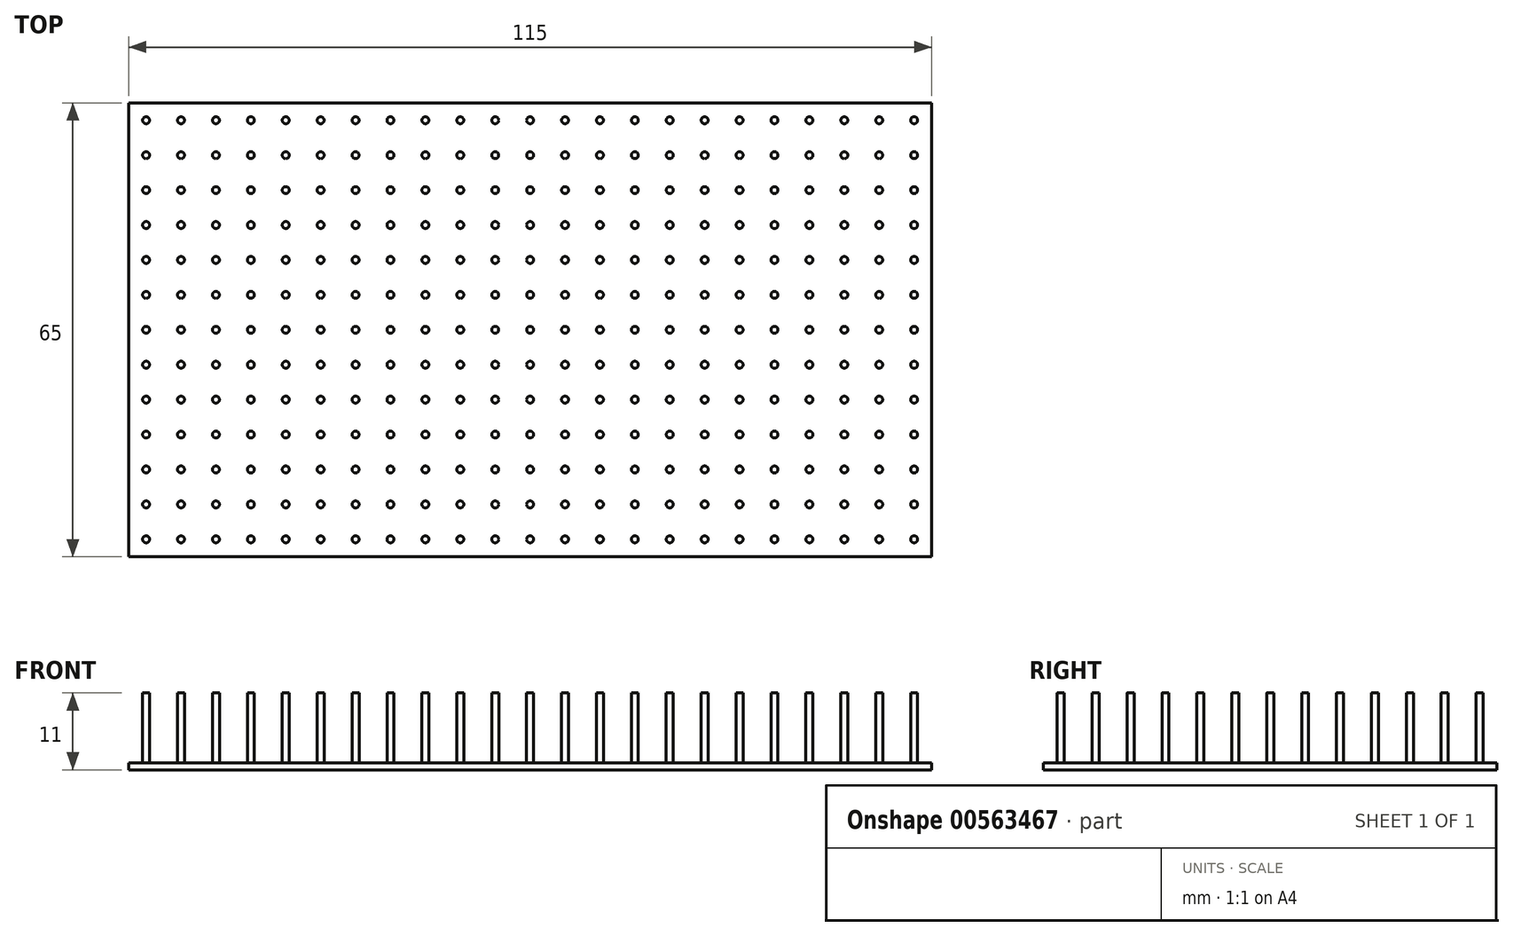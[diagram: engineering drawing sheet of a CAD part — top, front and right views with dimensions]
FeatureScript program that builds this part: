
annotation { "Feature Type Name" : "Feature", "Feature Type Description" : "" }
export const myFeature = defineFeature(function(context is Context, id is Id, definition is map)
    precondition{}
    {
        {
            var Q0;
            Q0=qCreatedBy(makeId("Top.planeOp"),FACE);
            var sketch = newSketch(context, id + "F0", { "sketchPlane" : qUnion([Q0])});
            skLineSegment(sketch, "E0.bottom", {"start": v(0, 0) * mm, "end": v(115, 0) * mm});
            skLineSegment(sketch, "E0.top", {"start": v(0, 65) * mm, "end": v(115, 65) * mm});
            skLineSegment(sketch, "E0.left", {"start": v(0, 0) * mm, "end": v(0, 65) * mm});
            skLineSegment(sketch, "E0.right", {"start": v(115, 0) * mm, "end": v(115, 65) * mm});
            skSolve(sketch);
        }
        {
            var Q0;
            Q0 = qSketchRegion(id + "F0", true);
            extrude(context, id + "F1", {"entities" : qUnion([Q0]), "depth" : 1 * mm, "offsetDistance" : 25 * mm});
        }
        {
            var Q0;
            Q0=makeQuery(id+"F1.opExtrude","CAP_FACE",FACE,{"disambiguationData":[OSD([sQuery(id+"F0.wireOp",EDGE,"E0.bottom"),sQuery(id+"F0.wireOp",EDGE,"E0.top"),sQuery(id+"F0.wireOp",EDGE,"E0.left"),sQuery(id+"F0.wireOp",EDGE,"E0.right")])],"isStart":false});
            var sketch = newSketch(context, id + "F2", { "sketchPlane" : qUnion([Q0])});
            skCircle(sketch, "E1", {"center": v(2.5, 2.5) * mm, "radius": 0.5 * mm});
            skCircle(sketch, "E2.0.1.0", {"center": v(2.5, 7.5) * mm, "radius": 0.5 * mm});
            skCircle(sketch, "E2.0.2.0", {"center": v(2.5, 12.5) * mm, "radius": 0.5 * mm});
            skCircle(sketch, "E2.0.3.0", {"center": v(2.5, 17.5) * mm, "radius": 0.5 * mm});
            skCircle(sketch, "E2.0.4.0", {"center": v(2.5, 22.5) * mm, "radius": 0.5 * mm});
            skCircle(sketch, "E2.0.5.0", {"center": v(2.5, 27.5) * mm, "radius": 0.5 * mm});
            skCircle(sketch, "E2.0.6.0", {"center": v(2.5, 32.5) * mm, "radius": 0.5 * mm});
            skCircle(sketch, "E2.0.7.0", {"center": v(2.5, 37.5) * mm, "radius": 0.5 * mm});
            skCircle(sketch, "E2.0.8.0", {"center": v(2.5, 42.5) * mm, "radius": 0.5 * mm});
            skCircle(sketch, "E2.0.9.0", {"center": v(2.5, 47.5) * mm, "radius": 0.5 * mm});
            skCircle(sketch, "E2.0.10.0", {"center": v(2.5, 52.5) * mm, "radius": 0.5 * mm});
            skCircle(sketch, "E2.0.11.0", {"center": v(2.5, 57.5) * mm, "radius": 0.5 * mm});
            skCircle(sketch, "E2.0.12.0", {"center": v(2.5, 62.5) * mm, "radius": 0.5 * mm});
            skCircle(sketch, "E2.1.0.0", {"center": v(7.5, 2.5) * mm, "radius": 0.5 * mm});
            skCircle(sketch, "E2.1.1.0", {"center": v(7.5, 7.5) * mm, "radius": 0.5 * mm});
            skCircle(sketch, "E2.1.2.0", {"center": v(7.5, 12.5) * mm, "radius": 0.5 * mm});
            skCircle(sketch, "E2.1.3.0", {"center": v(7.5, 17.5) * mm, "radius": 0.5 * mm});
            skCircle(sketch, "E2.1.4.0", {"center": v(7.5, 22.5) * mm, "radius": 0.5 * mm});
            skCircle(sketch, "E2.1.5.0", {"center": v(7.5, 27.5) * mm, "radius": 0.5 * mm});
            skCircle(sketch, "E2.1.6.0", {"center": v(7.5, 32.5) * mm, "radius": 0.5 * mm});
            skCircle(sketch, "E2.1.7.0", {"center": v(7.5, 37.5) * mm, "radius": 0.5 * mm});
            skCircle(sketch, "E2.1.8.0", {"center": v(7.5, 42.5) * mm, "radius": 0.5 * mm});
            skCircle(sketch, "E2.1.9.0", {"center": v(7.5, 47.5) * mm, "radius": 0.5 * mm});
            skCircle(sketch, "E2.1.10.0", {"center": v(7.5, 52.5) * mm, "radius": 0.5 * mm});
            skCircle(sketch, "E2.1.11.0", {"center": v(7.5, 57.5) * mm, "radius": 0.5 * mm});
            skCircle(sketch, "E2.1.12.0", {"center": v(7.5, 62.5) * mm, "radius": 0.5 * mm});
            skCircle(sketch, "E2.2.0.0", {"center": v(12.5, 2.5) * mm, "radius": 0.5 * mm});
            skCircle(sketch, "E2.2.1.0", {"center": v(12.5, 7.5) * mm, "radius": 0.5 * mm});
            skCircle(sketch, "E2.2.2.0", {"center": v(12.5, 12.5) * mm, "radius": 0.5 * mm});
            skCircle(sketch, "E2.2.3.0", {"center": v(12.5, 17.5) * mm, "radius": 0.5 * mm});
            skCircle(sketch, "E2.2.4.0", {"center": v(12.5, 22.5) * mm, "radius": 0.5 * mm});
            skCircle(sketch, "E2.2.5.0", {"center": v(12.5, 27.5) * mm, "radius": 0.5 * mm});
            skCircle(sketch, "E2.2.6.0", {"center": v(12.5, 32.5) * mm, "radius": 0.5 * mm});
            skCircle(sketch, "E2.2.7.0", {"center": v(12.5, 37.5) * mm, "radius": 0.5 * mm});
            skCircle(sketch, "E2.2.8.0", {"center": v(12.5, 42.5) * mm, "radius": 0.5 * mm});
            skCircle(sketch, "E2.2.9.0", {"center": v(12.5, 47.5) * mm, "radius": 0.5 * mm});
            skCircle(sketch, "E2.2.10.0", {"center": v(12.5, 52.5) * mm, "radius": 0.5 * mm});
            skCircle(sketch, "E2.2.11.0", {"center": v(12.5, 57.5) * mm, "radius": 0.5 * mm});
            skCircle(sketch, "E2.2.12.0", {"center": v(12.5, 62.5) * mm, "radius": 0.5 * mm});
            skCircle(sketch, "E2.3.0.0", {"center": v(17.5, 2.5) * mm, "radius": 0.5 * mm});
            skCircle(sketch, "E2.3.1.0", {"center": v(17.5, 7.5) * mm, "radius": 0.5 * mm});
            skCircle(sketch, "E2.3.2.0", {"center": v(17.5, 12.5) * mm, "radius": 0.5 * mm});
            skCircle(sketch, "E2.3.3.0", {"center": v(17.5, 17.5) * mm, "radius": 0.5 * mm});
            skCircle(sketch, "E2.3.4.0", {"center": v(17.5, 22.5) * mm, "radius": 0.5 * mm});
            skCircle(sketch, "E2.3.5.0", {"center": v(17.5, 27.5) * mm, "radius": 0.5 * mm});
            skCircle(sketch, "E2.3.6.0", {"center": v(17.5, 32.5) * mm, "radius": 0.5 * mm});
            skCircle(sketch, "E2.3.7.0", {"center": v(17.5, 37.5) * mm, "radius": 0.5 * mm});
            skCircle(sketch, "E2.3.8.0", {"center": v(17.5, 42.5) * mm, "radius": 0.5 * mm});
            skCircle(sketch, "E2.3.9.0", {"center": v(17.5, 47.5) * mm, "radius": 0.5 * mm});
            skCircle(sketch, "E2.3.10.0", {"center": v(17.5, 52.5) * mm, "radius": 0.5 * mm});
            skCircle(sketch, "E2.3.11.0", {"center": v(17.5, 57.5) * mm, "radius": 0.5 * mm});
            skCircle(sketch, "E2.3.12.0", {"center": v(17.5, 62.5) * mm, "radius": 0.5 * mm});
            skCircle(sketch, "E2.4.0.0", {"center": v(22.5, 2.5) * mm, "radius": 0.5 * mm});
            skCircle(sketch, "E2.4.1.0", {"center": v(22.5, 7.5) * mm, "radius": 0.5 * mm});
            skCircle(sketch, "E2.4.2.0", {"center": v(22.5, 12.5) * mm, "radius": 0.5 * mm});
            skCircle(sketch, "E2.4.3.0", {"center": v(22.5, 17.5) * mm, "radius": 0.5 * mm});
            skCircle(sketch, "E2.4.4.0", {"center": v(22.5, 22.5) * mm, "radius": 0.5 * mm});
            skCircle(sketch, "E2.4.5.0", {"center": v(22.5, 27.5) * mm, "radius": 0.5 * mm});
            skCircle(sketch, "E2.4.6.0", {"center": v(22.5, 32.5) * mm, "radius": 0.5 * mm});
            skCircle(sketch, "E2.4.7.0", {"center": v(22.5, 37.5) * mm, "radius": 0.5 * mm});
            skCircle(sketch, "E2.4.8.0", {"center": v(22.5, 42.5) * mm, "radius": 0.5 * mm});
            skCircle(sketch, "E2.4.9.0", {"center": v(22.5, 47.5) * mm, "radius": 0.5 * mm});
            skCircle(sketch, "E2.4.10.0", {"center": v(22.5, 52.5) * mm, "radius": 0.5 * mm});
            skCircle(sketch, "E2.4.11.0", {"center": v(22.5, 57.5) * mm, "radius": 0.5 * mm});
            skCircle(sketch, "E2.4.12.0", {"center": v(22.5, 62.5) * mm, "radius": 0.5 * mm});
            skCircle(sketch, "E2.5.0.0", {"center": v(27.5, 2.5) * mm, "radius": 0.5 * mm});
            skCircle(sketch, "E2.5.1.0", {"center": v(27.5, 7.5) * mm, "radius": 0.5 * mm});
            skCircle(sketch, "E2.5.2.0", {"center": v(27.5, 12.5) * mm, "radius": 0.5 * mm});
            skCircle(sketch, "E2.5.3.0", {"center": v(27.5, 17.5) * mm, "radius": 0.5 * mm});
            skCircle(sketch, "E2.5.4.0", {"center": v(27.5, 22.5) * mm, "radius": 0.5 * mm});
            skCircle(sketch, "E2.5.5.0", {"center": v(27.5, 27.5) * mm, "radius": 0.5 * mm});
            skCircle(sketch, "E2.5.6.0", {"center": v(27.5, 32.5) * mm, "radius": 0.5 * mm});
            skCircle(sketch, "E2.5.7.0", {"center": v(27.5, 37.5) * mm, "radius": 0.5 * mm});
            skCircle(sketch, "E2.5.8.0", {"center": v(27.5, 42.5) * mm, "radius": 0.5 * mm});
            skCircle(sketch, "E2.5.9.0", {"center": v(27.5, 47.5) * mm, "radius": 0.5 * mm});
            skCircle(sketch, "E2.5.10.0", {"center": v(27.5, 52.5) * mm, "radius": 0.5 * mm});
            skCircle(sketch, "E2.5.11.0", {"center": v(27.5, 57.5) * mm, "radius": 0.5 * mm});
            skCircle(sketch, "E2.5.12.0", {"center": v(27.5, 62.5) * mm, "radius": 0.5 * mm});
            skCircle(sketch, "E2.6.0.0", {"center": v(32.5, 2.5) * mm, "radius": 0.5 * mm});
            skCircle(sketch, "E2.6.1.0", {"center": v(32.5, 7.5) * mm, "radius": 0.5 * mm});
            skCircle(sketch, "E2.6.2.0", {"center": v(32.5, 12.5) * mm, "radius": 0.5 * mm});
            skCircle(sketch, "E2.6.3.0", {"center": v(32.5, 17.5) * mm, "radius": 0.5 * mm});
            skCircle(sketch, "E2.6.4.0", {"center": v(32.5, 22.5) * mm, "radius": 0.5 * mm});
            skCircle(sketch, "E2.6.5.0", {"center": v(32.5, 27.5) * mm, "radius": 0.5 * mm});
            skCircle(sketch, "E2.6.6.0", {"center": v(32.5, 32.5) * mm, "radius": 0.5 * mm});
            skCircle(sketch, "E2.6.7.0", {"center": v(32.5, 37.5) * mm, "radius": 0.5 * mm});
            skCircle(sketch, "E2.6.8.0", {"center": v(32.5, 42.5) * mm, "radius": 0.5 * mm});
            skCircle(sketch, "E2.6.9.0", {"center": v(32.5, 47.5) * mm, "radius": 0.5 * mm});
            skCircle(sketch, "E2.6.10.0", {"center": v(32.5, 52.5) * mm, "radius": 0.5 * mm});
            skCircle(sketch, "E2.6.11.0", {"center": v(32.5, 57.5) * mm, "radius": 0.5 * mm});
            skCircle(sketch, "E2.6.12.0", {"center": v(32.5, 62.5) * mm, "radius": 0.5 * mm});
            skCircle(sketch, "E2.7.0.0", {"center": v(37.5, 2.5) * mm, "radius": 0.5 * mm});
            skCircle(sketch, "E2.7.1.0", {"center": v(37.5, 7.5) * mm, "radius": 0.5 * mm});
            skCircle(sketch, "E2.7.2.0", {"center": v(37.5, 12.5) * mm, "radius": 0.5 * mm});
            skCircle(sketch, "E2.7.3.0", {"center": v(37.5, 17.5) * mm, "radius": 0.5 * mm});
            skCircle(sketch, "E2.7.4.0", {"center": v(37.5, 22.5) * mm, "radius": 0.5 * mm});
            skCircle(sketch, "E2.7.5.0", {"center": v(37.5, 27.5) * mm, "radius": 0.5 * mm});
            skCircle(sketch, "E2.7.6.0", {"center": v(37.5, 32.5) * mm, "radius": 0.5 * mm});
            skCircle(sketch, "E2.7.7.0", {"center": v(37.5, 37.5) * mm, "radius": 0.5 * mm});
            skCircle(sketch, "E2.7.8.0", {"center": v(37.5, 42.5) * mm, "radius": 0.5 * mm});
            skCircle(sketch, "E2.7.9.0", {"center": v(37.5, 47.5) * mm, "radius": 0.5 * mm});
            skCircle(sketch, "E2.7.10.0", {"center": v(37.5, 52.5) * mm, "radius": 0.5 * mm});
            skCircle(sketch, "E2.7.11.0", {"center": v(37.5, 57.5) * mm, "radius": 0.5 * mm});
            skCircle(sketch, "E2.7.12.0", {"center": v(37.5, 62.5) * mm, "radius": 0.5 * mm});
            skCircle(sketch, "E2.8.0.0", {"center": v(42.5, 2.5) * mm, "radius": 0.5 * mm});
            skCircle(sketch, "E2.8.1.0", {"center": v(42.5, 7.5) * mm, "radius": 0.5 * mm});
            skCircle(sketch, "E2.8.2.0", {"center": v(42.5, 12.5) * mm, "radius": 0.5 * mm});
            skCircle(sketch, "E2.8.3.0", {"center": v(42.5, 17.5) * mm, "radius": 0.5 * mm});
            skCircle(sketch, "E2.8.4.0", {"center": v(42.5, 22.5) * mm, "radius": 0.5 * mm});
            skCircle(sketch, "E2.8.5.0", {"center": v(42.5, 27.5) * mm, "radius": 0.5 * mm});
            skCircle(sketch, "E2.8.6.0", {"center": v(42.5, 32.5) * mm, "radius": 0.5 * mm});
            skCircle(sketch, "E2.8.7.0", {"center": v(42.5, 37.5) * mm, "radius": 0.5 * mm});
            skCircle(sketch, "E2.8.8.0", {"center": v(42.5, 42.5) * mm, "radius": 0.5 * mm});
            skCircle(sketch, "E2.8.9.0", {"center": v(42.5, 47.5) * mm, "radius": 0.5 * mm});
            skCircle(sketch, "E2.8.10.0", {"center": v(42.5, 52.5) * mm, "radius": 0.5 * mm});
            skCircle(sketch, "E2.8.11.0", {"center": v(42.5, 57.5) * mm, "radius": 0.5 * mm});
            skCircle(sketch, "E2.8.12.0", {"center": v(42.5, 62.5) * mm, "radius": 0.5 * mm});
            skCircle(sketch, "E2.9.0.0", {"center": v(47.5, 2.5) * mm, "radius": 0.5 * mm});
            skCircle(sketch, "E2.9.1.0", {"center": v(47.5, 7.5) * mm, "radius": 0.5 * mm});
            skCircle(sketch, "E2.9.2.0", {"center": v(47.5, 12.5) * mm, "radius": 0.5 * mm});
            skCircle(sketch, "E2.9.3.0", {"center": v(47.5, 17.5) * mm, "radius": 0.5 * mm});
            skCircle(sketch, "E2.9.4.0", {"center": v(47.5, 22.5) * mm, "radius": 0.5 * mm});
            skCircle(sketch, "E2.9.5.0", {"center": v(47.5, 27.5) * mm, "radius": 0.5 * mm});
            skCircle(sketch, "E2.9.6.0", {"center": v(47.5, 32.5) * mm, "radius": 0.5 * mm});
            skCircle(sketch, "E2.9.7.0", {"center": v(47.5, 37.5) * mm, "radius": 0.5 * mm});
            skCircle(sketch, "E2.9.8.0", {"center": v(47.5, 42.5) * mm, "radius": 0.5 * mm});
            skCircle(sketch, "E2.9.9.0", {"center": v(47.5, 47.5) * mm, "radius": 0.5 * mm});
            skCircle(sketch, "E2.9.10.0", {"center": v(47.5, 52.5) * mm, "radius": 0.5 * mm});
            skCircle(sketch, "E2.9.11.0", {"center": v(47.5, 57.5) * mm, "radius": 0.5 * mm});
            skCircle(sketch, "E2.9.12.0", {"center": v(47.5, 62.5) * mm, "radius": 0.5 * mm});
            skCircle(sketch, "E2.10.0.0", {"center": v(52.5, 2.5) * mm, "radius": 0.5 * mm});
            skCircle(sketch, "E2.10.1.0", {"center": v(52.5, 7.5) * mm, "radius": 0.5 * mm});
            skCircle(sketch, "E2.10.2.0", {"center": v(52.5, 12.5) * mm, "radius": 0.5 * mm});
            skCircle(sketch, "E2.10.3.0", {"center": v(52.5, 17.5) * mm, "radius": 0.5 * mm});
            skCircle(sketch, "E2.10.4.0", {"center": v(52.5, 22.5) * mm, "radius": 0.5 * mm});
            skCircle(sketch, "E2.10.5.0", {"center": v(52.5, 27.5) * mm, "radius": 0.5 * mm});
            skCircle(sketch, "E2.10.6.0", {"center": v(52.5, 32.5) * mm, "radius": 0.5 * mm});
            skCircle(sketch, "E2.10.7.0", {"center": v(52.5, 37.5) * mm, "radius": 0.5 * mm});
            skCircle(sketch, "E2.10.8.0", {"center": v(52.5, 42.5) * mm, "radius": 0.5 * mm});
            skCircle(sketch, "E2.10.9.0", {"center": v(52.5, 47.5) * mm, "radius": 0.5 * mm});
            skCircle(sketch, "E2.10.10.0", {"center": v(52.5, 52.5) * mm, "radius": 0.5 * mm});
            skCircle(sketch, "E2.10.11.0", {"center": v(52.5, 57.5) * mm, "radius": 0.5 * mm});
            skCircle(sketch, "E2.10.12.0", {"center": v(52.5, 62.5) * mm, "radius": 0.5 * mm});
            skCircle(sketch, "E2.11.0.0", {"center": v(57.5, 2.5) * mm, "radius": 0.5 * mm});
            skCircle(sketch, "E2.11.1.0", {"center": v(57.5, 7.5) * mm, "radius": 0.5 * mm});
            skCircle(sketch, "E2.11.2.0", {"center": v(57.5, 12.5) * mm, "radius": 0.5 * mm});
            skCircle(sketch, "E2.11.3.0", {"center": v(57.5, 17.5) * mm, "radius": 0.5 * mm});
            skCircle(sketch, "E2.11.4.0", {"center": v(57.5, 22.5) * mm, "radius": 0.5 * mm});
            skCircle(sketch, "E2.11.5.0", {"center": v(57.5, 27.5) * mm, "radius": 0.5 * mm});
            skCircle(sketch, "E2.11.6.0", {"center": v(57.5, 32.5) * mm, "radius": 0.5 * mm});
            skCircle(sketch, "E2.11.7.0", {"center": v(57.5, 37.5) * mm, "radius": 0.5 * mm});
            skCircle(sketch, "E2.11.8.0", {"center": v(57.5, 42.5) * mm, "radius": 0.5 * mm});
            skCircle(sketch, "E2.11.9.0", {"center": v(57.5, 47.5) * mm, "radius": 0.5 * mm});
            skCircle(sketch, "E2.11.10.0", {"center": v(57.5, 52.5) * mm, "radius": 0.5 * mm});
            skCircle(sketch, "E2.11.11.0", {"center": v(57.5, 57.5) * mm, "radius": 0.5 * mm});
            skCircle(sketch, "E2.11.12.0", {"center": v(57.5, 62.5) * mm, "radius": 0.5 * mm});
            skCircle(sketch, "E2.12.0.0", {"center": v(62.5, 2.5) * mm, "radius": 0.5 * mm});
            skCircle(sketch, "E2.12.1.0", {"center": v(62.5, 7.5) * mm, "radius": 0.5 * mm});
            skCircle(sketch, "E2.12.2.0", {"center": v(62.5, 12.5) * mm, "radius": 0.5 * mm});
            skCircle(sketch, "E2.12.3.0", {"center": v(62.5, 17.5) * mm, "radius": 0.5 * mm});
            skCircle(sketch, "E2.12.4.0", {"center": v(62.5, 22.5) * mm, "radius": 0.5 * mm});
            skCircle(sketch, "E2.12.5.0", {"center": v(62.5, 27.5) * mm, "radius": 0.5 * mm});
            skCircle(sketch, "E2.12.6.0", {"center": v(62.5, 32.5) * mm, "radius": 0.5 * mm});
            skCircle(sketch, "E2.12.7.0", {"center": v(62.5, 37.5) * mm, "radius": 0.5 * mm});
            skCircle(sketch, "E2.12.8.0", {"center": v(62.5, 42.5) * mm, "radius": 0.5 * mm});
            skCircle(sketch, "E2.12.9.0", {"center": v(62.5, 47.5) * mm, "radius": 0.5 * mm});
            skCircle(sketch, "E2.12.10.0", {"center": v(62.5, 52.5) * mm, "radius": 0.5 * mm});
            skCircle(sketch, "E2.12.11.0", {"center": v(62.5, 57.5) * mm, "radius": 0.5 * mm});
            skCircle(sketch, "E2.12.12.0", {"center": v(62.5, 62.5) * mm, "radius": 0.5 * mm});
            skCircle(sketch, "E2.13.0.0", {"center": v(67.5, 2.5) * mm, "radius": 0.5 * mm});
            skCircle(sketch, "E2.13.1.0", {"center": v(67.5, 7.5) * mm, "radius": 0.5 * mm});
            skCircle(sketch, "E2.13.2.0", {"center": v(67.5, 12.5) * mm, "radius": 0.5 * mm});
            skCircle(sketch, "E2.13.3.0", {"center": v(67.5, 17.5) * mm, "radius": 0.5 * mm});
            skCircle(sketch, "E2.13.4.0", {"center": v(67.5, 22.5) * mm, "radius": 0.5 * mm});
            skCircle(sketch, "E2.13.5.0", {"center": v(67.5, 27.5) * mm, "radius": 0.5 * mm});
            skCircle(sketch, "E2.13.6.0", {"center": v(67.5, 32.5) * mm, "radius": 0.5 * mm});
            skCircle(sketch, "E2.13.7.0", {"center": v(67.5, 37.5) * mm, "radius": 0.5 * mm});
            skCircle(sketch, "E2.13.8.0", {"center": v(67.5, 42.5) * mm, "radius": 0.5 * mm});
            skCircle(sketch, "E2.13.9.0", {"center": v(67.5, 47.5) * mm, "radius": 0.5 * mm});
            skCircle(sketch, "E2.13.10.0", {"center": v(67.5, 52.5) * mm, "radius": 0.5 * mm});
            skCircle(sketch, "E2.13.11.0", {"center": v(67.5, 57.5) * mm, "radius": 0.5 * mm});
            skCircle(sketch, "E2.13.12.0", {"center": v(67.5, 62.5) * mm, "radius": 0.5 * mm});
            skCircle(sketch, "E2.14.0.0", {"center": v(72.5, 2.5) * mm, "radius": 0.5 * mm});
            skCircle(sketch, "E2.14.1.0", {"center": v(72.5, 7.5) * mm, "radius": 0.5 * mm});
            skCircle(sketch, "E2.14.2.0", {"center": v(72.5, 12.5) * mm, "radius": 0.5 * mm});
            skCircle(sketch, "E2.14.3.0", {"center": v(72.5, 17.5) * mm, "radius": 0.5 * mm});
            skCircle(sketch, "E2.14.4.0", {"center": v(72.5, 22.5) * mm, "radius": 0.5 * mm});
            skCircle(sketch, "E2.14.5.0", {"center": v(72.5, 27.5) * mm, "radius": 0.5 * mm});
            skCircle(sketch, "E2.14.6.0", {"center": v(72.5, 32.5) * mm, "radius": 0.5 * mm});
            skCircle(sketch, "E2.14.7.0", {"center": v(72.5, 37.5) * mm, "radius": 0.5 * mm});
            skCircle(sketch, "E2.14.8.0", {"center": v(72.5, 42.5) * mm, "radius": 0.5 * mm});
            skCircle(sketch, "E2.14.9.0", {"center": v(72.5, 47.5) * mm, "radius": 0.5 * mm});
            skCircle(sketch, "E2.14.10.0", {"center": v(72.5, 52.5) * mm, "radius": 0.5 * mm});
            skCircle(sketch, "E2.14.11.0", {"center": v(72.5, 57.5) * mm, "radius": 0.5 * mm});
            skCircle(sketch, "E2.14.12.0", {"center": v(72.5, 62.5) * mm, "radius": 0.5 * mm});
            skCircle(sketch, "E2.15.0.0", {"center": v(77.5, 2.5) * mm, "radius": 0.5 * mm});
            skCircle(sketch, "E2.15.1.0", {"center": v(77.5, 7.5) * mm, "radius": 0.5 * mm});
            skCircle(sketch, "E2.15.2.0", {"center": v(77.5, 12.5) * mm, "radius": 0.5 * mm});
            skCircle(sketch, "E2.15.3.0", {"center": v(77.5, 17.5) * mm, "radius": 0.5 * mm});
            skCircle(sketch, "E2.15.4.0", {"center": v(77.5, 22.5) * mm, "radius": 0.5 * mm});
            skCircle(sketch, "E2.15.5.0", {"center": v(77.5, 27.5) * mm, "radius": 0.5 * mm});
            skCircle(sketch, "E2.15.6.0", {"center": v(77.5, 32.5) * mm, "radius": 0.5 * mm});
            skCircle(sketch, "E2.15.7.0", {"center": v(77.5, 37.5) * mm, "radius": 0.5 * mm});
            skCircle(sketch, "E2.15.8.0", {"center": v(77.5, 42.5) * mm, "radius": 0.5 * mm});
            skCircle(sketch, "E2.15.9.0", {"center": v(77.5, 47.5) * mm, "radius": 0.5 * mm});
            skCircle(sketch, "E2.15.10.0", {"center": v(77.5, 52.5) * mm, "radius": 0.5 * mm});
            skCircle(sketch, "E2.15.11.0", {"center": v(77.5, 57.5) * mm, "radius": 0.5 * mm});
            skCircle(sketch, "E2.15.12.0", {"center": v(77.5, 62.5) * mm, "radius": 0.5 * mm});
            skCircle(sketch, "E2.16.0.0", {"center": v(82.5, 2.5) * mm, "radius": 0.5 * mm});
            skCircle(sketch, "E2.16.1.0", {"center": v(82.5, 7.5) * mm, "radius": 0.5 * mm});
            skCircle(sketch, "E2.16.2.0", {"center": v(82.5, 12.5) * mm, "radius": 0.5 * mm});
            skCircle(sketch, "E2.16.3.0", {"center": v(82.5, 17.5) * mm, "radius": 0.5 * mm});
            skCircle(sketch, "E2.16.4.0", {"center": v(82.5, 22.5) * mm, "radius": 0.5 * mm});
            skCircle(sketch, "E2.16.5.0", {"center": v(82.5, 27.5) * mm, "radius": 0.5 * mm});
            skCircle(sketch, "E2.16.6.0", {"center": v(82.5, 32.5) * mm, "radius": 0.5 * mm});
            skCircle(sketch, "E2.16.7.0", {"center": v(82.5, 37.5) * mm, "radius": 0.5 * mm});
            skCircle(sketch, "E2.16.8.0", {"center": v(82.5, 42.5) * mm, "radius": 0.5 * mm});
            skCircle(sketch, "E2.16.9.0", {"center": v(82.5, 47.5) * mm, "radius": 0.5 * mm});
            skCircle(sketch, "E2.16.10.0", {"center": v(82.5, 52.5) * mm, "radius": 0.5 * mm});
            skCircle(sketch, "E2.16.11.0", {"center": v(82.5, 57.5) * mm, "radius": 0.5 * mm});
            skCircle(sketch, "E2.16.12.0", {"center": v(82.5, 62.5) * mm, "radius": 0.5 * mm});
            skCircle(sketch, "E2.17.0.0", {"center": v(87.5, 2.5) * mm, "radius": 0.5 * mm});
            skCircle(sketch, "E2.17.1.0", {"center": v(87.5, 7.5) * mm, "radius": 0.5 * mm});
            skCircle(sketch, "E2.17.2.0", {"center": v(87.5, 12.5) * mm, "radius": 0.5 * mm});
            skCircle(sketch, "E2.17.3.0", {"center": v(87.5, 17.5) * mm, "radius": 0.5 * mm});
            skCircle(sketch, "E2.17.4.0", {"center": v(87.5, 22.5) * mm, "radius": 0.5 * mm});
            skCircle(sketch, "E2.17.5.0", {"center": v(87.5, 27.5) * mm, "radius": 0.5 * mm});
            skCircle(sketch, "E2.17.6.0", {"center": v(87.5, 32.5) * mm, "radius": 0.5 * mm});
            skCircle(sketch, "E2.17.7.0", {"center": v(87.5, 37.5) * mm, "radius": 0.5 * mm});
            skCircle(sketch, "E2.17.8.0", {"center": v(87.5, 42.5) * mm, "radius": 0.5 * mm});
            skCircle(sketch, "E2.17.9.0", {"center": v(87.5, 47.5) * mm, "radius": 0.5 * mm});
            skCircle(sketch, "E2.17.10.0", {"center": v(87.5, 52.5) * mm, "radius": 0.5 * mm});
            skCircle(sketch, "E2.17.11.0", {"center": v(87.5, 57.5) * mm, "radius": 0.5 * mm});
            skCircle(sketch, "E2.17.12.0", {"center": v(87.5, 62.5) * mm, "radius": 0.5 * mm});
            skCircle(sketch, "E2.18.0.0", {"center": v(92.5, 2.5) * mm, "radius": 0.5 * mm});
            skCircle(sketch, "E2.18.1.0", {"center": v(92.5, 7.5) * mm, "radius": 0.5 * mm});
            skCircle(sketch, "E2.18.2.0", {"center": v(92.5, 12.5) * mm, "radius": 0.5 * mm});
            skCircle(sketch, "E2.18.3.0", {"center": v(92.5, 17.5) * mm, "radius": 0.5 * mm});
            skCircle(sketch, "E2.18.4.0", {"center": v(92.5, 22.5) * mm, "radius": 0.5 * mm});
            skCircle(sketch, "E2.18.5.0", {"center": v(92.5, 27.5) * mm, "radius": 0.5 * mm});
            skCircle(sketch, "E2.18.6.0", {"center": v(92.5, 32.5) * mm, "radius": 0.5 * mm});
            skCircle(sketch, "E2.18.7.0", {"center": v(92.5, 37.5) * mm, "radius": 0.5 * mm});
            skCircle(sketch, "E2.18.8.0", {"center": v(92.5, 42.5) * mm, "radius": 0.5 * mm});
            skCircle(sketch, "E2.18.9.0", {"center": v(92.5, 47.5) * mm, "radius": 0.5 * mm});
            skCircle(sketch, "E2.18.10.0", {"center": v(92.5, 52.5) * mm, "radius": 0.5 * mm});
            skCircle(sketch, "E2.18.11.0", {"center": v(92.5, 57.5) * mm, "radius": 0.5 * mm});
            skCircle(sketch, "E2.18.12.0", {"center": v(92.5, 62.5) * mm, "radius": 0.5 * mm});
            skCircle(sketch, "E2.19.0.0", {"center": v(97.5, 2.5) * mm, "radius": 0.5 * mm});
            skCircle(sketch, "E2.19.1.0", {"center": v(97.5, 7.5) * mm, "radius": 0.5 * mm});
            skCircle(sketch, "E2.19.2.0", {"center": v(97.5, 12.5) * mm, "radius": 0.5 * mm});
            skCircle(sketch, "E2.19.3.0", {"center": v(97.5, 17.5) * mm, "radius": 0.5 * mm});
            skCircle(sketch, "E2.19.4.0", {"center": v(97.5, 22.5) * mm, "radius": 0.5 * mm});
            skCircle(sketch, "E2.19.5.0", {"center": v(97.5, 27.5) * mm, "radius": 0.5 * mm});
            skCircle(sketch, "E2.19.6.0", {"center": v(97.5, 32.5) * mm, "radius": 0.5 * mm});
            skCircle(sketch, "E2.19.7.0", {"center": v(97.5, 37.5) * mm, "radius": 0.5 * mm});
            skCircle(sketch, "E2.19.8.0", {"center": v(97.5, 42.5) * mm, "radius": 0.5 * mm});
            skCircle(sketch, "E2.19.9.0", {"center": v(97.5, 47.5) * mm, "radius": 0.5 * mm});
            skCircle(sketch, "E2.19.10.0", {"center": v(97.5, 52.5) * mm, "radius": 0.5 * mm});
            skCircle(sketch, "E2.19.11.0", {"center": v(97.5, 57.5) * mm, "radius": 0.5 * mm});
            skCircle(sketch, "E2.19.12.0", {"center": v(97.5, 62.5) * mm, "radius": 0.5 * mm});
            skCircle(sketch, "E2.20.0.0", {"center": v(102.5, 2.5) * mm, "radius": 0.5 * mm});
            skCircle(sketch, "E2.20.1.0", {"center": v(102.5, 7.5) * mm, "radius": 0.5 * mm});
            skCircle(sketch, "E2.20.2.0", {"center": v(102.5, 12.5) * mm, "radius": 0.5 * mm});
            skCircle(sketch, "E2.20.3.0", {"center": v(102.5, 17.5) * mm, "radius": 0.5 * mm});
            skCircle(sketch, "E2.20.4.0", {"center": v(102.5, 22.5) * mm, "radius": 0.5 * mm});
            skCircle(sketch, "E2.20.5.0", {"center": v(102.5, 27.5) * mm, "radius": 0.5 * mm});
            skCircle(sketch, "E2.20.6.0", {"center": v(102.5, 32.5) * mm, "radius": 0.5 * mm});
            skCircle(sketch, "E2.20.7.0", {"center": v(102.5, 37.5) * mm, "radius": 0.5 * mm});
            skCircle(sketch, "E2.20.8.0", {"center": v(102.5, 42.5) * mm, "radius": 0.5 * mm});
            skCircle(sketch, "E2.20.9.0", {"center": v(102.5, 47.5) * mm, "radius": 0.5 * mm});
            skCircle(sketch, "E2.20.10.0", {"center": v(102.5, 52.5) * mm, "radius": 0.5 * mm});
            skCircle(sketch, "E2.20.11.0", {"center": v(102.5, 57.5) * mm, "radius": 0.5 * mm});
            skCircle(sketch, "E2.20.12.0", {"center": v(102.5, 62.5) * mm, "radius": 0.5 * mm});
            skCircle(sketch, "E2.21.0.0", {"center": v(107.5, 2.5) * mm, "radius": 0.5 * mm});
            skCircle(sketch, "E2.21.1.0", {"center": v(107.5, 7.5) * mm, "radius": 0.5 * mm});
            skCircle(sketch, "E2.21.2.0", {"center": v(107.5, 12.5) * mm, "radius": 0.5 * mm});
            skCircle(sketch, "E2.21.3.0", {"center": v(107.5, 17.5) * mm, "radius": 0.5 * mm});
            skCircle(sketch, "E2.21.4.0", {"center": v(107.5, 22.5) * mm, "radius": 0.5 * mm});
            skCircle(sketch, "E2.21.5.0", {"center": v(107.5, 27.5) * mm, "radius": 0.5 * mm});
            skCircle(sketch, "E2.21.6.0", {"center": v(107.5, 32.5) * mm, "radius": 0.5 * mm});
            skCircle(sketch, "E2.21.7.0", {"center": v(107.5, 37.5) * mm, "radius": 0.5 * mm});
            skCircle(sketch, "E2.21.8.0", {"center": v(107.5, 42.5) * mm, "radius": 0.5 * mm});
            skCircle(sketch, "E2.21.9.0", {"center": v(107.5, 47.5) * mm, "radius": 0.5 * mm});
            skCircle(sketch, "E2.21.10.0", {"center": v(107.5, 52.5) * mm, "radius": 0.5 * mm});
            skCircle(sketch, "E2.21.11.0", {"center": v(107.5, 57.5) * mm, "radius": 0.5 * mm});
            skCircle(sketch, "E2.21.12.0", {"center": v(107.5, 62.5) * mm, "radius": 0.5 * mm});
            skCircle(sketch, "E2.22.0.0", {"center": v(112.5, 2.5) * mm, "radius": 0.5 * mm});
            skCircle(sketch, "E2.22.1.0", {"center": v(112.5, 7.5) * mm, "radius": 0.5 * mm});
            skCircle(sketch, "E2.22.2.0", {"center": v(112.5, 12.5) * mm, "radius": 0.5 * mm});
            skCircle(sketch, "E2.22.3.0", {"center": v(112.5, 17.5) * mm, "radius": 0.5 * mm});
            skCircle(sketch, "E2.22.4.0", {"center": v(112.5, 22.5) * mm, "radius": 0.5 * mm});
            skCircle(sketch, "E2.22.5.0", {"center": v(112.5, 27.5) * mm, "radius": 0.5 * mm});
            skCircle(sketch, "E2.22.6.0", {"center": v(112.5, 32.5) * mm, "radius": 0.5 * mm});
            skCircle(sketch, "E2.22.7.0", {"center": v(112.5, 37.5) * mm, "radius": 0.5 * mm});
            skCircle(sketch, "E2.22.8.0", {"center": v(112.5, 42.5) * mm, "radius": 0.5 * mm});
            skCircle(sketch, "E2.22.9.0", {"center": v(112.5, 47.5) * mm, "radius": 0.5 * mm});
            skCircle(sketch, "E2.22.10.0", {"center": v(112.5, 52.5) * mm, "radius": 0.5 * mm});
            skCircle(sketch, "E2.22.11.0", {"center": v(112.5, 57.5) * mm, "radius": 0.5 * mm});
            skCircle(sketch, "E2.22.12.0", {"center": v(112.5, 62.5) * mm, "radius": 0.5 * mm});
            skLineSegment(sketch, "E2.direction1", {"start": v(2.5, 2.5) * mm, "end": v(7.5, 2.5) * mm, "construction": true});
            skLineSegment(sketch, "E2.direction2", {"start": v(2.5, 2.5) * mm, "end": v(2.5, 7.5) * mm, "construction": true});
            skSolve(sketch);
        }
        {
            var Q0;
            Q0 = qSketchRegion(id + "F2", true);
            extrude(context, id + "F3", {"entities" : qUnion([Q0]), "operationType" : NewBodyOperationType.ADD, "depth" : 10 * mm, "offsetDistance" : 25 * mm});
        }
    });
